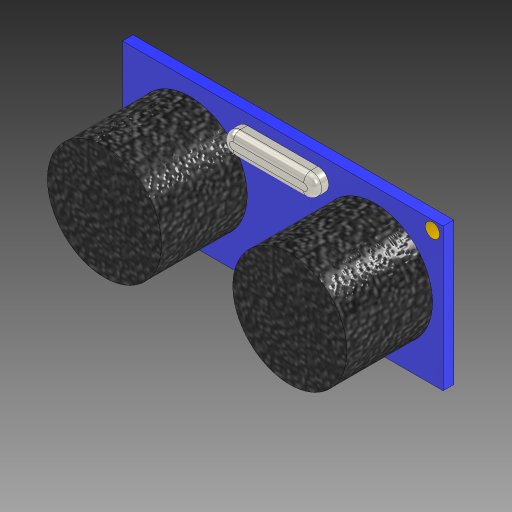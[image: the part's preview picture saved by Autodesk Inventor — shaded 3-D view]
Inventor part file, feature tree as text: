
AUTODESK INVENTOR PART (.ipt)
format: ipt  version: 2023 (Build 270158000, 158)  size: 264,704 bytes
history: native  units: mm
features: extrude x5, sketch x5, other x1, fillet x1
ambient origin geometry x8: Origin, YZ Plane, XZ Plane, XY Plane, X Axis, Y Axis, Z Axis, Center Point
bodies: Body1 (feature_tree)
feature tree (12):
  other  "Těleso1"
  extrude  "Vysunutí1"  Depth=45.0mm
  extrude  "Vysunutí2"  Depth=20.0mm
  extrude  "Vysunutí3"  Depth=1.5mm TaperAngle=0.0deg
  fillet  "Zaoblení1"  Radius=16.0mm
  extrude  "Vysunutí4"  Depth=16.0mm
  extrude  "Vysunutí5"  Depth=26.0mm
  sketch  "Náčrt1"
  sketch  "Náčrt2"
  sketch  "Náčrt3"
  sketch  "Náčrt4"
  sketch  "Náčrt6"
